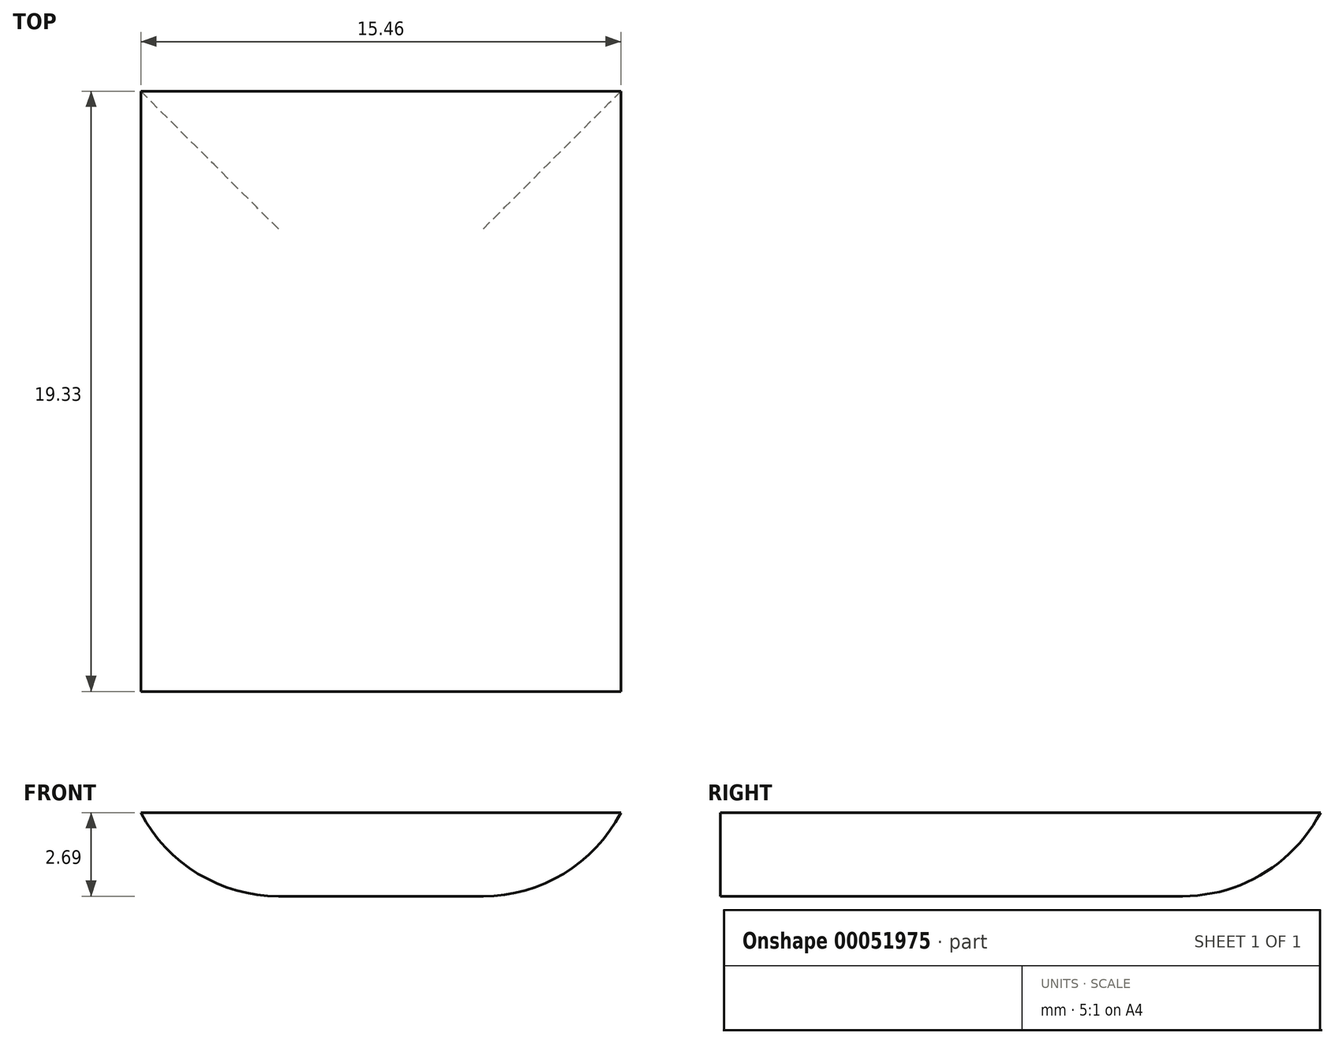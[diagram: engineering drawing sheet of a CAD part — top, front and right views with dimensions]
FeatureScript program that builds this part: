
annotation { "Feature Type Name" : "Feature", "Feature Type Description" : "" }
export const myFeature = defineFeature(function(context is Context, id is Id, definition is map)
    precondition{}
    {
        {
            var Q0;
            Q0=qCreatedBy(makeId("Top.planeOp"),FACE);
            var sketch = newSketch(context, id + "F0", { "sketchPlane" : qUnion([Q0])});
            skLineSegment(sketch, "E0.bottom", {"start": v(-40.26, 33.34) * mm, "end": v(-24.8, 33.34) * mm});
            skLineSegment(sketch, "E0.top", {"start": v(-40.26, 14.01) * mm, "end": v(-24.8, 14.01) * mm});
            skLineSegment(sketch, "E0.left", {"start": v(-40.26, 33.34) * mm, "end": v(-40.26, 14.01) * mm});
            skLineSegment(sketch, "E0.right", {"start": v(-24.8, 33.34) * mm, "end": v(-24.8, 14.01) * mm});
            skSolve(sketch);
        }
        {
            var Q0;
            Q0 = qSketchRegion(id + "F0", true);
            extrude(context, id + "F1", {"entities" : qUnion([Q0]), "depth" : 2.69 * mm});
        }
        {
            var Q0;
            Q0=makeQuery(id+"F1.opExtrude","CAP_EDGE",EDGE,{"disambiguationData":[OSD([sQuery(id+"F0.wireOp",EDGE,"E0.bottom")])],"isStart":true});
            var Q1;
            Q1=makeQuery(id+"F1.opExtrude","CAP_EDGE",EDGE,{"disambiguationData":[OSD([sQuery(id+"F0.wireOp",EDGE,"E0.right")])],"isStart":true});
            var Q2;
            Q2=makeQuery(id+"F1.opExtrude","CAP_EDGE",EDGE,{"disambiguationData":[OSD([sQuery(id+"F0.wireOp",EDGE,"E0.left")])],"isStart":true});
            fillet(context, id + "F2", {"entities" : qUnion([Q0, Q1, Q2]), "radius" : 5 * mm, "tangentPropagation" : true, "allowEdgeOverflow" : false});
        }
    });
